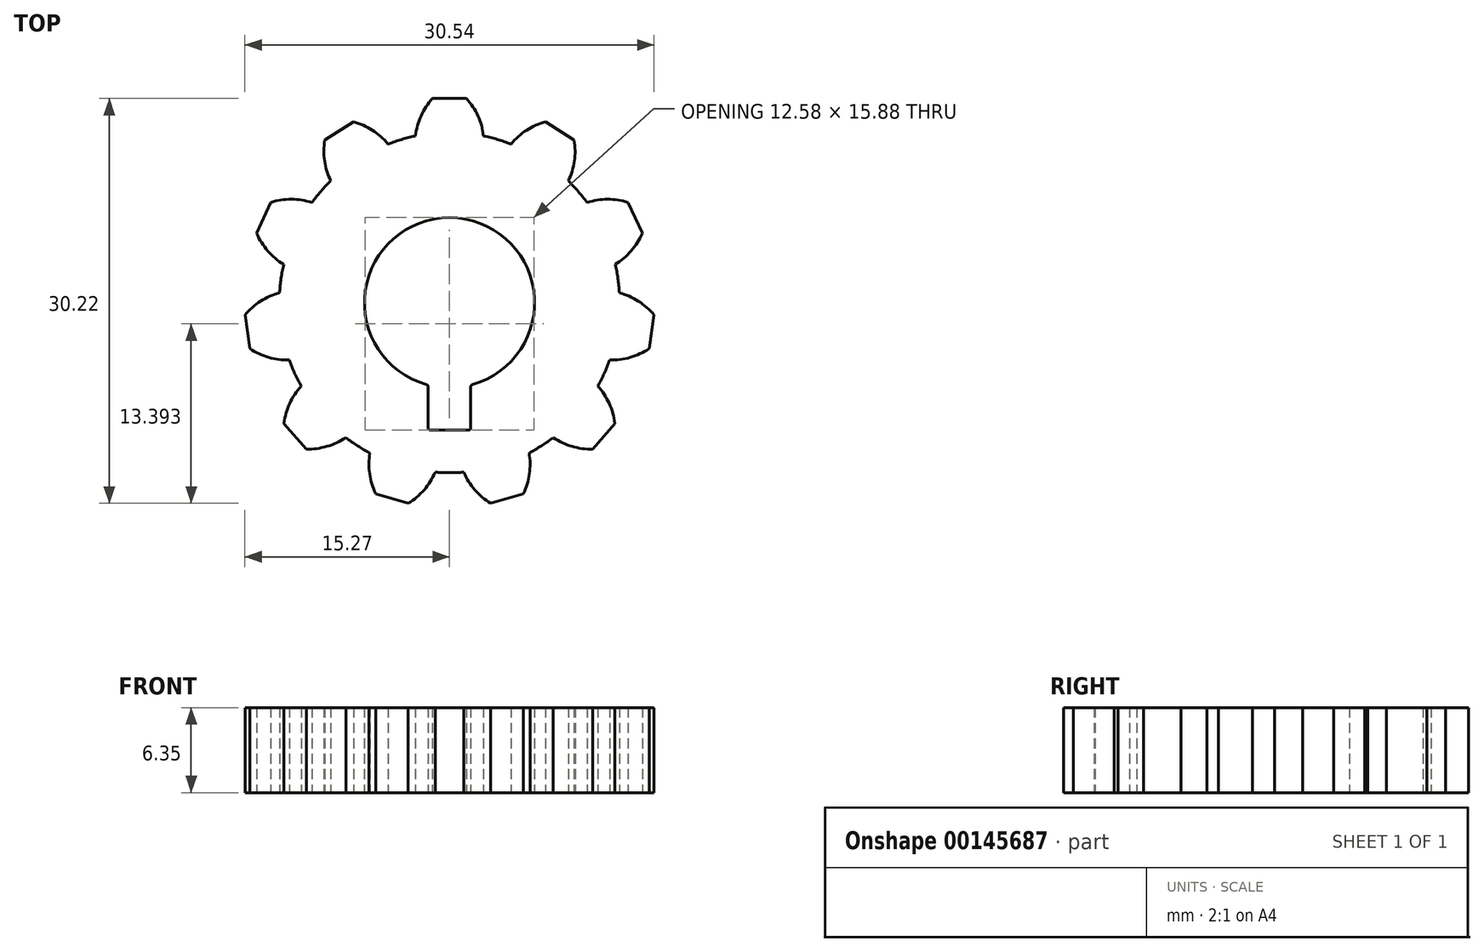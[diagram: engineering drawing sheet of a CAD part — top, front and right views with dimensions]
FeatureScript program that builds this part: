
annotation { "Feature Type Name" : "Feature", "Feature Type Description" : "" }
export const myFeature = defineFeature(function(context is Context, id is Id, definition is map)
    precondition{}
    {
        {
            var Q0;
            Q0=qCreatedBy(makeId("Top.planeOp"),FACE);
            var sketch = newSketch(context, id + "F0", { "sketchPlane" : qUnion([Q0])});
            skArc(sketch, "E0", {"start": v(-8.86, 9.1) * mm, "mid": v(-9.6, 8.32) * mm, "end": v(-10.26, 7.48) * mm, "construction": true});
            skArc(sketch, "E1", {"start": v(-1.27, 15.24) * mm, "mid": v(-2.12, 13.94) * mm, "end": v(-2.54, 12.44) * mm});
            skLineSegment(sketch, "E2", {"start": v(-1.27, 15.24) * mm, "end": v(1.27, 15.24) * mm});
            skArc(sketch, "E3", {"start": v(2.54, 12.44) * mm, "mid": v(2.12, 13.94) * mm, "end": v(1.27, 15.24) * mm});
            skLineSegment(sketch, "E4", {"start": v(0, 15.24) * mm, "end": v(0, 0) * mm, "construction": true});
            skLineSegment(sketch, "E5", {"start": v(-2.54, 12.44) * mm, "end": v(2.54, 12.44) * mm, "construction": true});
            skLineSegment(sketch, "E6.1.0", {"start": v(-9.3, 12.13) * mm, "end": v(-7.17, 13.5) * mm});
            skArc(sketch, "E6.1.1", {"start": v(-9.3, 12.13) * mm, "mid": v(-9.32, 10.58) * mm, "end": v(-8.86, 9.1) * mm});
            skArc(sketch, "E6.1.2", {"start": v(-4.6, 11.84) * mm, "mid": v(-5.75, 12.87) * mm, "end": v(-7.17, 13.5) * mm});
            skLineSegment(sketch, "E6.2.0", {"start": v(-14.4, 5.18) * mm, "end": v(-13.34, 7.49) * mm});
            skArc(sketch, "E6.2.1", {"start": v(-14.4, 5.18) * mm, "mid": v(-13.56, 3.86) * mm, "end": v(-12.37, 2.86) * mm});
            skArc(sketch, "E6.2.2", {"start": v(-10.26, 7.48) * mm, "mid": v(-11.8, 7.72) * mm, "end": v(-13.34, 7.49) * mm});
            skLineSegment(sketch, "E6.3.0", {"start": v(-14.9, -3.43) * mm, "end": v(-15.27, -0.91) * mm});
            skArc(sketch, "E6.3.1", {"start": v(-14.9, -3.43) * mm, "mid": v(-13.5, -4.08) * mm, "end": v(-11.96, -4.29) * mm});
            skArc(sketch, "E6.3.2", {"start": v(-12.68, 0.74) * mm, "mid": v(-14.1, 0.12) * mm, "end": v(-15.27, -0.91) * mm});
            skLineSegment(sketch, "E6.4.0", {"start": v(-10.69, -10.94) * mm, "end": v(-12.35, -9.02) * mm});
            skArc(sketch, "E6.4.1", {"start": v(-10.69, -10.94) * mm, "mid": v(-9.15, -10.73) * mm, "end": v(-7.74, -10.07) * mm});
            skArc(sketch, "E6.4.2", {"start": v(-11.07, -6.23) * mm, "mid": v(-11.92, -7.53) * mm, "end": v(-12.35, -9.02) * mm});
            skLineSegment(sketch, "E6.5.0", {"start": v(-3.08, -14.98) * mm, "end": v(-5.51, -14.26) * mm});
            skArc(sketch, "E6.5.1", {"start": v(-3.08, -14.98) * mm, "mid": v(-1.9, -13.97) * mm, "end": v(-1.07, -12.65) * mm});
            skArc(sketch, "E6.5.2", {"start": v(-5.94, -11.22) * mm, "mid": v(-5.96, -12.78) * mm, "end": v(-5.51, -14.26) * mm});
            skArc(sketch, "E7", {"start": v(-8.86, 9.1) * mm, "mid": v(-9.6, 8.32) * mm, "end": v(-10.26, 7.48) * mm});
            skArc(sketch, "E8.trimOffspring", {"start": v(-2.54, 12.44) * mm, "mid": v(-3.58, 12.19) * mm, "end": v(-4.6, 11.84) * mm});
            skArc(sketch, "E9.trimOffspring", {"start": v(4.6, 11.84) * mm, "mid": v(3.58, 12.19) * mm, "end": v(2.54, 12.44) * mm});
            skArc(sketch, "E10.trimOffspring", {"start": v(-7.74, -10.07) * mm, "mid": v(-6.87, -10.68) * mm, "end": v(-5.94, -11.22) * mm});
            skArc(sketch, "E11.trimOffspring", {"start": v(-11.96, -4.29) * mm, "mid": v(-11.55, -5.28) * mm, "end": v(-11.07, -6.23) * mm});
            skArc(sketch, "E12.trimOffspring", {"start": v(-12.37, 2.86) * mm, "mid": v(-12.57, 1.8) * mm, "end": v(-12.68, 0.74) * mm});
            skLineSegment(sketch, "E13.1.6.0", {"start": v(5.51, -14.26) * mm, "end": v(3.08, -14.98) * mm});
            skArc(sketch, "E13.3.6.0", {"start": v(5.51, -14.26) * mm, "mid": v(5.96, -12.78) * mm, "end": v(5.94, -11.22) * mm});
            skArc(sketch, "E13.7.6.0", {"start": v(1.07, -12.65) * mm, "mid": v(1.9, -13.97) * mm, "end": v(3.08, -14.98) * mm});
            skLineSegment(sketch, "E13.1.7.0", {"start": v(12.35, -9.02) * mm, "end": v(10.69, -10.94) * mm});
            skArc(sketch, "E13.3.7.0", {"start": v(12.35, -9.02) * mm, "mid": v(11.92, -7.53) * mm, "end": v(11.07, -6.23) * mm});
            skArc(sketch, "E13.7.7.0", {"start": v(7.74, -10.07) * mm, "mid": v(9.15, -10.73) * mm, "end": v(10.69, -10.94) * mm});
            skLineSegment(sketch, "E13.1.8.0", {"start": v(15.27, -0.91) * mm, "end": v(14.9, -3.43) * mm});
            skArc(sketch, "E13.3.8.0", {"start": v(15.27, -0.91) * mm, "mid": v(14.1, 0.12) * mm, "end": v(12.68, 0.74) * mm});
            skArc(sketch, "E13.7.8.0", {"start": v(11.96, -4.29) * mm, "mid": v(13.5, -4.08) * mm, "end": v(14.9, -3.43) * mm});
            skLineSegment(sketch, "E13.1.9.0", {"start": v(13.34, 7.49) * mm, "end": v(14.4, 5.18) * mm});
            skArc(sketch, "E13.3.9.0", {"start": v(13.34, 7.49) * mm, "mid": v(11.8, 7.72) * mm, "end": v(10.26, 7.48) * mm});
            skArc(sketch, "E13.7.9.0", {"start": v(12.37, 2.86) * mm, "mid": v(13.56, 3.86) * mm, "end": v(14.4, 5.18) * mm});
            skLineSegment(sketch, "E13.1.10.0", {"start": v(7.17, 13.5) * mm, "end": v(9.3, 12.13) * mm});
            skArc(sketch, "E13.3.10.0", {"start": v(7.17, 13.5) * mm, "mid": v(5.75, 12.87) * mm, "end": v(4.6, 11.84) * mm});
            skArc(sketch, "E13.7.10.0", {"start": v(8.86, 9.1) * mm, "mid": v(9.32, 10.58) * mm, "end": v(9.3, 12.13) * mm});
            skArc(sketch, "E14", {"start": v(1.72, -6.11) * mm, "mid": v(0, 6.35) * mm, "end": v(-1.72, -6.11) * mm});
            skLineSegment(sketch, "E15", {"start": v(-1.59, -6.28) * mm, "end": v(-1.59, -9.35) * mm});
            skLineSegment(sketch, "E16", {"start": v(-1.4, -9.53) * mm, "end": v(1.4, -9.53) * mm});
            skLineSegment(sketch, "E17", {"start": v(1.59, -9.35) * mm, "end": v(1.59, -6.28) * mm});
            skLineSegment(sketch, "E18", {"start": v(0, 0) * mm, "end": v(0, -9.53) * mm, "construction": true});
            skPoint(sketch, "E19.visualSharp", {"position": v(-1.59, -6.15) * mm});
            skArc(sketch, "E19.filletArc", {"start": v(-1.59, -6.28) * mm, "mid": v(-1.62, -6.18) * mm, "end": v(-1.72, -6.11) * mm});
            skPoint(sketch, "E20.visualSharp", {"position": v(1.59, -6.15) * mm});
            skArc(sketch, "E20.filletArc", {"start": v(1.72, -6.11) * mm, "mid": v(1.62, -6.18) * mm, "end": v(1.59, -6.28) * mm});
            skPoint(sketch, "E21.visualSharp", {"position": v(-1.59, -9.53) * mm});
            skArc(sketch, "E21.filletArc", {"start": v(-1.59, -9.35) * mm, "mid": v(-1.54, -9.47) * mm, "end": v(-1.4, -9.53) * mm});
            skPoint(sketch, "E22.visualSharp", {"position": v(1.59, -9.53) * mm});
            skArc(sketch, "E22.filletArc", {"start": v(1.4, -9.53) * mm, "mid": v(1.54, -9.47) * mm, "end": v(1.59, -9.35) * mm});
            skArc(sketch, "E23.trimOffspring", {"start": v(-12.37, 2.86) * mm, "mid": v(-12.57, 1.8) * mm, "end": v(-12.68, 0.74) * mm, "construction": true});
            skArc(sketch, "E24.trimOffspring", {"start": v(-11.96, -4.29) * mm, "mid": v(-11.55, -5.28) * mm, "end": v(-11.07, -6.23) * mm, "construction": true});
            skArc(sketch, "E25.trimOffspring", {"start": v(-7.74, -10.07) * mm, "mid": v(-6.87, -10.68) * mm, "end": v(-5.94, -11.22) * mm, "construction": true});
            skArc(sketch, "E26.trimOffspring", {"start": v(-1.07, -12.65) * mm, "mid": v(0, -12.7) * mm, "end": v(1.07, -12.65) * mm, "construction": true});
            skArc(sketch, "E27.trimOffspring", {"start": v(-1.07, -12.65) * mm, "mid": v(0, -12.7) * mm, "end": v(1.07, -12.65) * mm});
            skArc(sketch, "E28.trimOffspring", {"start": v(5.94, -11.22) * mm, "mid": v(6.87, -10.68) * mm, "end": v(7.74, -10.07) * mm, "construction": true});
            skArc(sketch, "E29.trimOffspring", {"start": v(5.94, -11.22) * mm, "mid": v(6.87, -10.68) * mm, "end": v(7.74, -10.07) * mm});
            skArc(sketch, "E30.trimOffspring", {"start": v(11.07, -6.23) * mm, "mid": v(11.55, -5.28) * mm, "end": v(11.96, -4.29) * mm, "construction": true});
            skArc(sketch, "E31.trimOffspring", {"start": v(11.07, -6.23) * mm, "mid": v(11.55, -5.28) * mm, "end": v(11.96, -4.29) * mm});
            skArc(sketch, "E32.trimOffspring", {"start": v(12.68, 0.74) * mm, "mid": v(12.57, 1.8) * mm, "end": v(12.37, 2.86) * mm, "construction": true});
            skArc(sketch, "E33.trimOffspring", {"start": v(12.68, 0.74) * mm, "mid": v(12.57, 1.8) * mm, "end": v(12.37, 2.86) * mm});
            skArc(sketch, "E34.trimOffspring", {"start": v(10.26, 7.48) * mm, "mid": v(9.6, 8.32) * mm, "end": v(8.86, 9.1) * mm, "construction": true});
            skArc(sketch, "E35.trimOffspring", {"start": v(10.26, 7.48) * mm, "mid": v(9.6, 8.32) * mm, "end": v(8.86, 9.1) * mm});
            skArc(sketch, "E36.trimOffspring", {"start": v(4.6, 11.84) * mm, "mid": v(0, 12.7) * mm, "end": v(-4.6, 11.84) * mm, "construction": true});
            skSolve(sketch);
        }
        {
            var Q0;
            Q0 = qSketchRegion(id + "F0", true);
            extrude(context, id + "F1", {"entities" : qUnion([Q0]), "depth" : 6.35 * mm});
        }
    });
